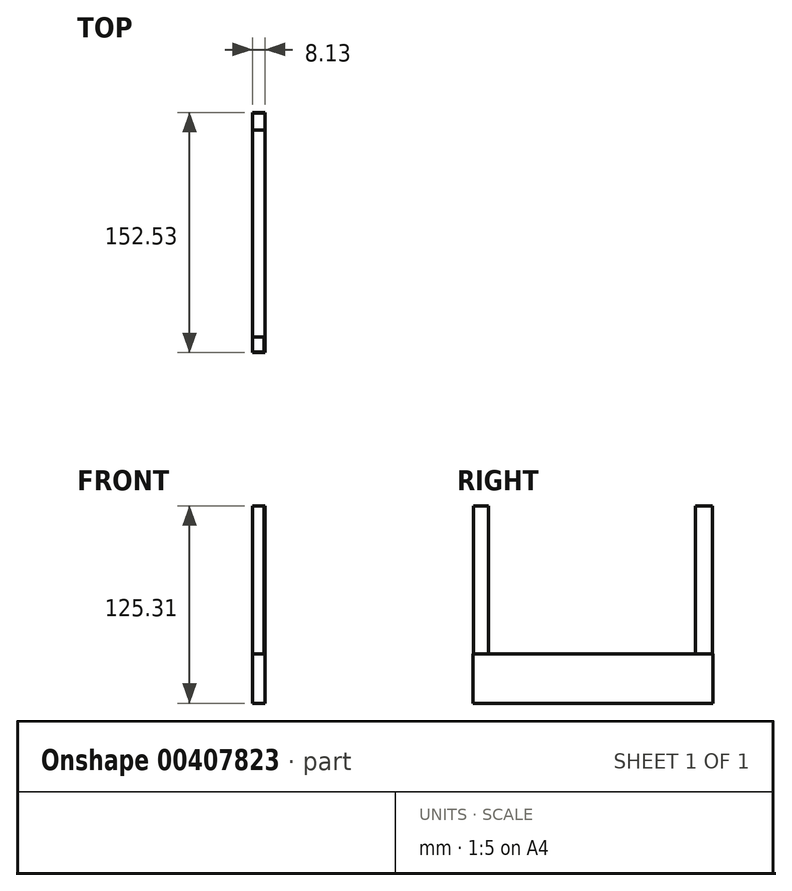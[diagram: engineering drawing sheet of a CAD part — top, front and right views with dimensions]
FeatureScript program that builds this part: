
annotation { "Feature Type Name" : "Feature", "Feature Type Description" : "" }
export const myFeature = defineFeature(function(context is Context, id is Id, definition is map)
    precondition{}
    {
        {
            var Q0;
            Q0=qCreatedBy(makeId("Right.planeOp"),FACE);
            var sketch = newSketch(context, id + "F0", { "sketchPlane" : qUnion([Q0])});
            skLineSegment(sketch, "E0", {"start": v(-76.46, 0) * mm, "end": v(76.07, 0) * mm});
            skLineSegment(sketch, "E1", {"start": v(76.07, 0) * mm, "end": v(76.07, -31.33) * mm});
            skLineSegment(sketch, "E2", {"start": v(76.07, -31.33) * mm, "end": v(-76.27, -31.33) * mm});
            skLineSegment(sketch, "E3", {"start": v(-76.27, -31.33) * mm, "end": v(-76.46, 0) * mm});
            skSolve(sketch);
        }
        {
            var Q0;
            Q0 = qSketchRegion(id + "F0", true);
            extrude(context, id + "F1", {"entities" : qUnion([Q0]), "depth" : 8.13 * mm});
        }
        {
            var Q0;
            Q0=qCreatedBy(makeId("Top.planeOp"),FACE);
            var sketch = newSketch(context, id + "F2", { "sketchPlane" : qUnion([Q0])});
            skLineSegment(sketch, "E4", {"start": v(0, -76.03) * mm, "end": v(7.38, -76.03) * mm});
            skLineSegment(sketch, "E5", {"start": v(7.38, -76.03) * mm, "end": v(7.38, -66.65) * mm});
            skLineSegment(sketch, "E6", {"start": v(7.38, -66.65) * mm, "end": v(0, -66.65) * mm});
            skLineSegment(sketch, "E7", {"start": v(0, -66.65) * mm, "end": v(0, -76.03) * mm});
            skLineSegment(sketch, "E8", {"start": v(0, 64.87) * mm, "end": v(7.95, 64.87) * mm});
            skPoint(sketch, "E8.startSnap0", {"position": v(0, -71.34) * mm});
            skLineSegment(sketch, "E9", {"start": v(7.95, 64.87) * mm, "end": v(7.95, 75.7) * mm});
            skLineSegment(sketch, "E10", {"start": v(7.95, 75.7) * mm, "end": v(0, 75.7) * mm});
            skLineSegment(sketch, "E11", {"start": v(0, 75.7) * mm, "end": v(0, 64.87) * mm});
            skSolve(sketch);
        }
        {
            var Q0;
            Q0 = qSketchRegion(id + "F2", true);
            extrude(context, id + "F3", {"entities" : qUnion([Q0]), "operationType" : NewBodyOperationType.ADD, "depth" : 93.98 * mm});
        }
    });
